# Revit family: Дверь RI 44 одностворчатая
name_source: partatom
category: Окна
revit_build: Autodesk Revit 2016 (Build: 20160314_0715(x64)
units: mm (PartAtom-declared; Revit-internal decimal feet)

## family parameters
Всегда вертикально = Да
Заголовок OmniClass = Windows
Номер OmniClass = 23.30.20.00
Общий = Нет
Основа = Стена
При загрузке вырезать с полостями = Нет
Точка расчета площади = Нет

## types (1)
- Дверь RI 44 одностворчатая
    ADSK_Версия Revit = Revit 2016
    ADSK_Единица измерения = шт.
    ADSK_Наименование краткое = Дверь RI 44 одностворчатая
    Rед = 1.0000 (м²·K)/Вт
    Rпрофиля = 1.0000 (м²·K)/Вт
    Rстеклопакета = 1.0000 (м²·K)/Вт
    URL = http://www.realit.ru
    λ краевой зоны стеклопакета = 0.0000 (м²·K)/Вт
    Аналитическая конструкция = <Нет>
    Высота = 0 мм
    Высота подоконника по умолчанию = 50 мм
    Замыкание стены = По основе
    Изготовитель = REALIT
    Левая = Нет
    Материал-Отлив = REALIT_Отлив_Белый
    Материал-Подоконник = REALIT_ПВХ_Белый
    Материал-Рама = REALIT_Профиль_RAL 9016
    Материал-Стеклопакет = REALIT_Стекло
    Монтажный зазор.Боковой = 20 мм
    Наименование = Дверь RI 44 одностворчатая
    Правая = Да
    Примерная высота = 0 мм
    Примерная ширина = 0 мм
    Рама.Высота профиля = 67 мм
    Рама.Ширина профиля = 44 мм
    Створка.Высота низ.профиля = 137 мм
    Створка.Высота профиля = 84 мм
    Створка.Ширина профиля = 44 мм
    Стеклопакет.Толщина = 26 мм
    Толщина стеклопакета = 26
    Угол в плане 30° = Нет
    Угол в плане 90° = Да
    Цвет профиля = RAL 9016
    Ширина = 0 мм

## geometry (parser evidence)
native form markers: Blend x2, Sweep x1
no freeform markers — native parametric forms only
